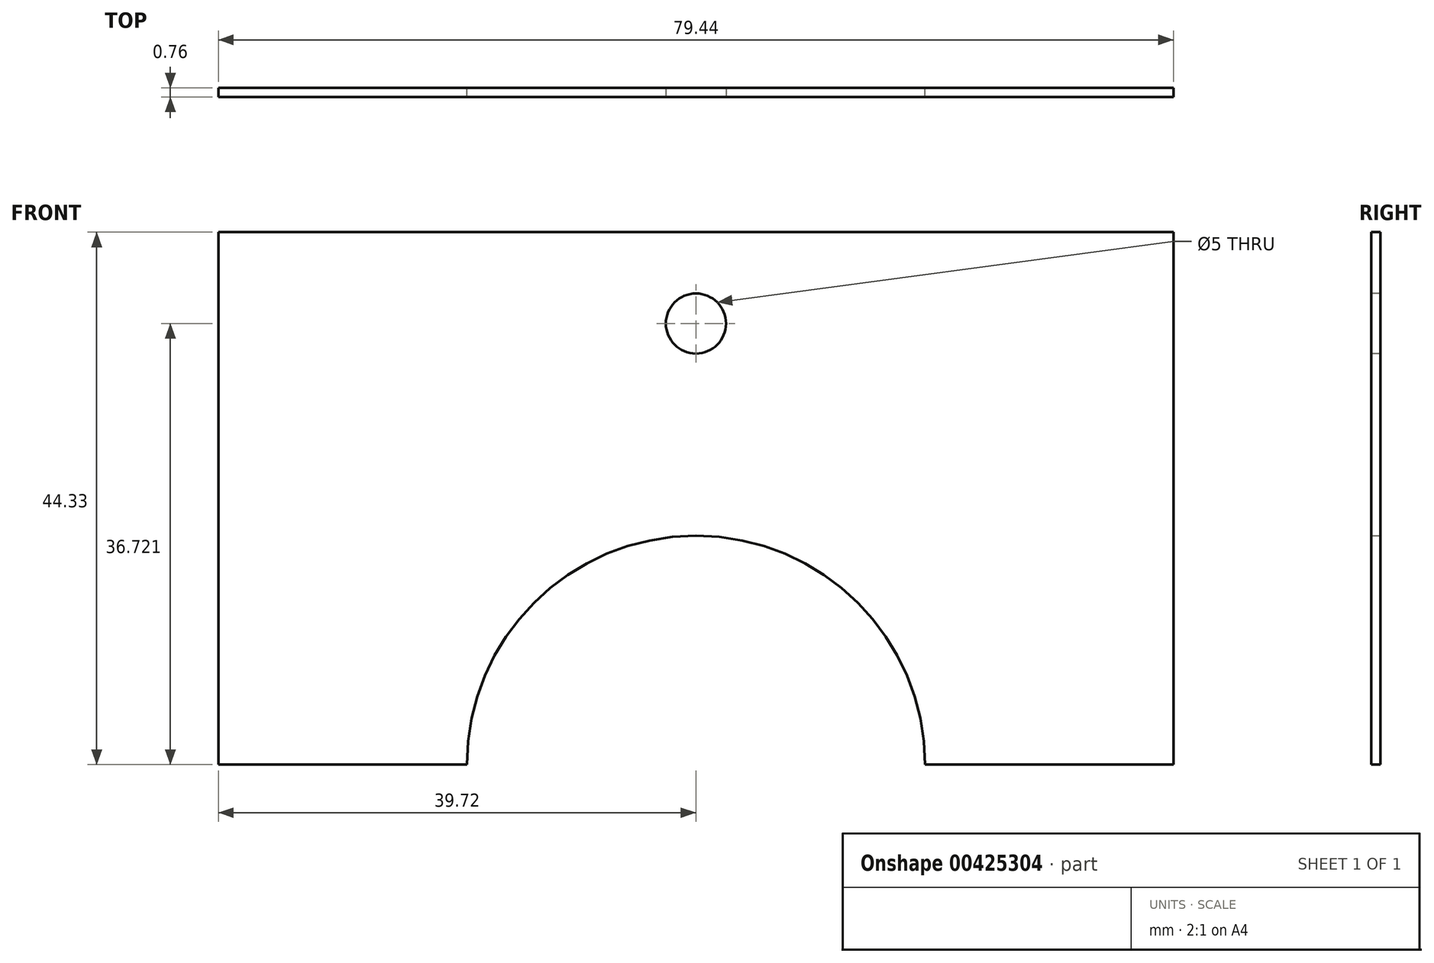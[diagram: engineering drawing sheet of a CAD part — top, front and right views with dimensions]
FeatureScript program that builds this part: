
annotation { "Feature Type Name" : "Feature", "Feature Type Description" : "" }
export const myFeature = defineFeature(function(context is Context, id is Id, definition is map)
    precondition{}
    {
        {
            var Q0;
            Q0=qCreatedBy(makeId("Front.planeOp"),FACE);
            var sketch = newSketch(context, id + "F0", { "sketchPlane" : qUnion([Q0])});
            skLineSegment(sketch, "E0.bottom", {"start": v(0, 0) * mm, "end": v(20.67, 0) * mm});
            skLineSegment(sketch, "E0.top", {"start": v(0, 44.33) * mm, "end": v(79.44, 44.33) * mm});
            skLineSegment(sketch, "E0.left", {"start": v(0, 0) * mm, "end": v(0, 44.33) * mm});
            skLineSegment(sketch, "E0.right", {"start": v(79.44, 0) * mm, "end": v(79.44, 44.33) * mm});
            skArc(sketch, "E1", {"start": v(58.77, 0) * mm, "mid": v(39.72, 19.05) * mm, "end": v(20.67, 0) * mm});
            skLineSegment(sketch, "E2.trimOffspring", {"start": v(58.77, 0) * mm, "end": v(79.44, 0) * mm});
            skSolve(sketch);
        }
        {
            var Q0;
            Q0=makeQuery(id+"F0.imprint","IMPRINT",FACE,{"disambiguationData":[TD([[makeQuery(id+"F0.imprint","IMPRINT",EDGE,{"derivedFrom":sQuery(id+"F0.wireOp",EDGE,"E0.bottom")}),1.0]])]});
            extrude(context, id + "F1", {"entities" : qUnion([Q0]), "depth" : 0.76 * mm});
        }
        {
            var Q0;
            Q0=makeQuery(id+"F1.opExtrude","CAP_FACE",FACE,{"disambiguationData":[OSD([sQuery(id+"F0.wireOp",EDGE,"E0.bottom"),sQuery(id+"F0.wireOp",EDGE,"E0.top"),sQuery(id+"F0.wireOp",EDGE,"E0.left"),sQuery(id+"F0.wireOp",EDGE,"E0.right"),sQuery(id+"F0.wireOp",EDGE,"E1"),sQuery(id+"F0.wireOp",EDGE,"E2.trimOffspring")])],"isStart":false});
            var sketch = newSketch(context, id + "F2", { "sketchPlane" : qUnion([Q0])});
            skPoint(sketch, "E3", {"position": v(39.72, 36.72) * mm});
            skPoint(sketch, "E3.positionSnap0", {"position": v(39.72, 44.33) * mm});
            skSolve(sketch);
        }
        {
            var Q0;
            Q0=sQuery(id+"F2.wireOp",VERTEX,"E3");
            var Q1;
            Q1=makeQuery(id+"F1.opExtrude","SWEPT_BODY",BODY,{"disambiguationData":[OSD([sQuery(id+"F0.wireOp",EDGE,"E0.bottom"),sQuery(id+"F0.wireOp",EDGE,"E0.top"),sQuery(id+"F0.wireOp",EDGE,"E0.left"),sQuery(id+"F0.wireOp",EDGE,"E0.right"),sQuery(id+"F0.wireOp",EDGE,"E1"),sQuery(id+"F0.wireOp",EDGE,"E2.trimOffspring")])]});
            hole(context, id + "F3", {"style" : HoleStyle.SIMPLE, "endStyle" : HoleEndStyle.THROUGH, "standardTappedOrClearance" : lookupTablePath({ "standard" : "ISO", "size" : "5", "type" : "Drilled" }), "standardBlindInLast" : lookupTablePath({ "standard" : "ISO", "size" : "5", "type" : "Drilled" }), "holeDiameter" : 5 * mm, "tappedDepth" : 91.5 * mm, "tapClearance" : 3, "locations" : qUnion([Q0]), "scope" : qUnion([Q1])});
        }
    });
